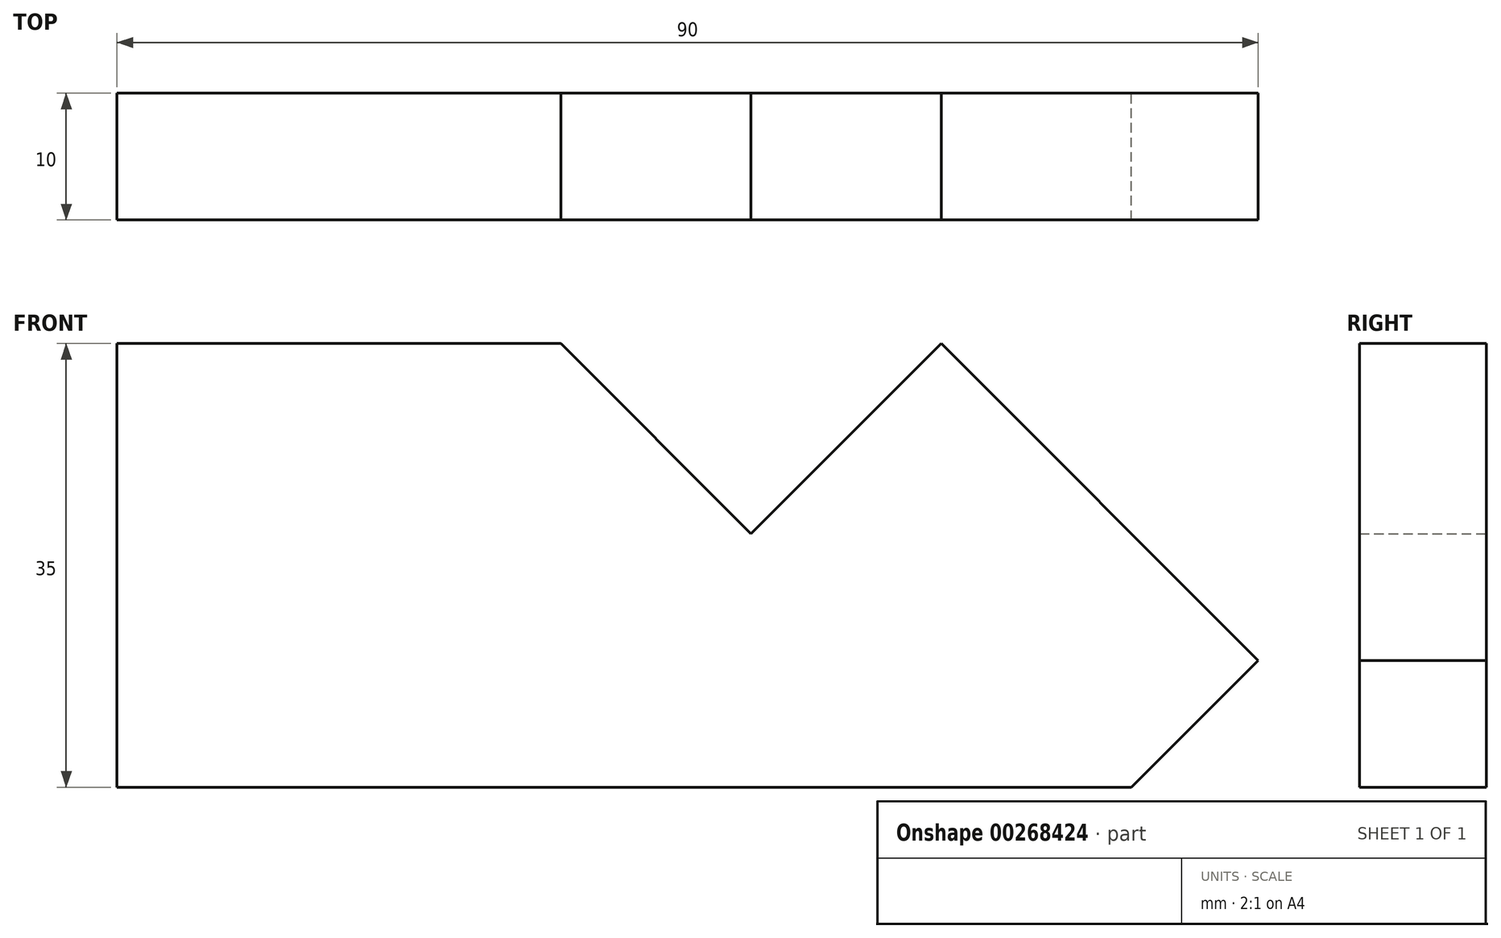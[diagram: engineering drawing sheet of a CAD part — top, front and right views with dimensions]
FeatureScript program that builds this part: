
annotation { "Feature Type Name" : "Feature", "Feature Type Description" : "" }
export const myFeature = defineFeature(function(context is Context, id is Id, definition is map)
    precondition{}
    {
        {
            var Q0;
            Q0=qCreatedBy(makeId("Front.planeOp"),FACE);
            var sketch = newSketch(context, id + "F0", { "sketchPlane" : qUnion([Q0])});
            skLineSegment(sketch, "E0", {"start": v(0, 0) * mm, "end": v(0, 35) * mm});
            skLineSegment(sketch, "E1", {"start": v(0, 35) * mm, "end": v(35, 35) * mm});
            skLineSegment(sketch, "E2", {"start": v(0, 0) * mm, "end": v(80, 0) * mm});
            skLineSegment(sketch, "E3", {"start": v(80, 0) * mm, "end": v(90, 10) * mm});
            skLineSegment(sketch, "E4", {"start": v(35, 35) * mm, "end": v(50, 20) * mm});
            skLineSegment(sketch, "E5", {"start": v(50, 20) * mm, "end": v(65, 35) * mm});
            skLineSegment(sketch, "E6", {"start": v(65, 35) * mm, "end": v(90, 10) * mm});
            skSolve(sketch);
        }
        {
            var Q0;
            Q0 = qSketchRegion(id + "F0", true);
            extrude(context, id + "F1", {"entities" : qUnion([Q0]), "depth" : 10 * mm});
        }
    });
